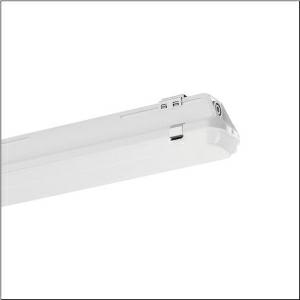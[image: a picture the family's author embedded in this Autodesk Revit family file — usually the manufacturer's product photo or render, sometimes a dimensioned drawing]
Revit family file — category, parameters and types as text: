
# Revit family: monsun_r__21_emergency_51fb20dl447k3h_3ee9
name_source: partatom
category: Lighting Fixtures
units: mm (PartAtom-declared; Revit-internal decimal feet)

## family parameters
Cut with Voids When Loaded = No
Host = Face
Light Source = No
Part Type = Normal
Room Calculation Point = No
Round Connector Dimension = Use Diameter
Shared = No

## types (1)
- --- (1 x LED, 840 lm, 6.2 W, 4000K)
    Apparent Load = 6 VA
    CIE Flux Codes = 45 75 93 94 100
    Color Rendering = 80
    Color Temperature = 4000K
    Default Elevation = 1800 mm
    Description = Monsun® 21 emergency, damp-proof luminaire, chain hanger, primary optical cover: enclosure, of PC, light emission: direct distribution, primary light characteristic: symmetric, installation type: vertical mounting, horizontal mounting, surface-mounted, suspended mounting, LED, rated luminous flux: 4.320lm, luminous efficacy: 162lm/W, light colour: 840, colour temperature: 4000K, control gear: DALI 2, with terminal, 5-pole, max. 2.5mm², mains connection: 220..240V, AC, 50/60Hz, rated input power: 30W, control gear: single battery element, battery: LiFePO4, 9Ah, housing, of glass-fibre reinforced plastic, uncoated, bright grey, incl. chain hanger, length: 1.299mm, width: 90mm, height: 88mm, clip for enclosure, of stainless steel (V2A), ceiling mounting element, of stainless steel (V2A), chain hanger, of stainless steel (V2A), protection rating (complete): IP66, insulation class (complete): insulation class I (protective earthing), certification: CE, UKCA, protection symbol: D, impact resistance: IK08, permissible operating ambient temperature: +5..+25°C, standard: EN 50419, EN 60598-2-1, corresponds to IFS (International Featured Standards) requirements for safety and quality in the food industry, for indoor or canopied outdoor use, no direct snow, no direct sun, no direct rain, LABS conformity tested according to VDMA 24364:2018-05, contact your sales advisor before using the luminaires in applications with unclear chemical exposure, large temperature fluctuations or condensation-forming humidity, packaging unit: 1 piece
    Height = 88 mm
    Lamp = 1 x LED
    Lamp Light Flux = 840 lm
    Lamp Power = 6.2 W
    Lamp count = 1
    Length = 1299 mm
    Luminous efficacy = 135 lm/W
    Manufacturer = Siteco
    ModVariant = No
    Model = 51FB20DL447K3H
    Mounting Place = Ceiling
    Mounting Type = Surface mounted
    Number of Poles = 1
    OnlyDefault = Yes
    Power Factor = 1
    Product Name = Monsun® 21 emergency
    Product group = damp-proof luminaire
    ProductGroupID = 300
    Protection Class = Protection class I
    Protection Degree = IP 66
    RLX_Detail_Level = 1
    RLX_Emergency_Light_Flux = 0 lm
    RLX_Emergency_Type = 0
    RLX_Emergency_Type_DB = No
    RlxData = <blob elided: 93705 chars, md5=52b667b2>
    Socket = socket
    Standby Power = 0 W
    System Light Flux = 840 lm
    System Power = 6 W
    Type Comments = : 3 h
    Type Image = l_1319656.jpg
    URL = http://relux.com
    VarID = @adj_022280
    Voltage = 0 V
    Weight = 0.00 kg
    Width = 90 mm

## geometry (parser evidence)
native form markers: Blend x4, Sweep x11
no freeform markers — native parametric forms only
